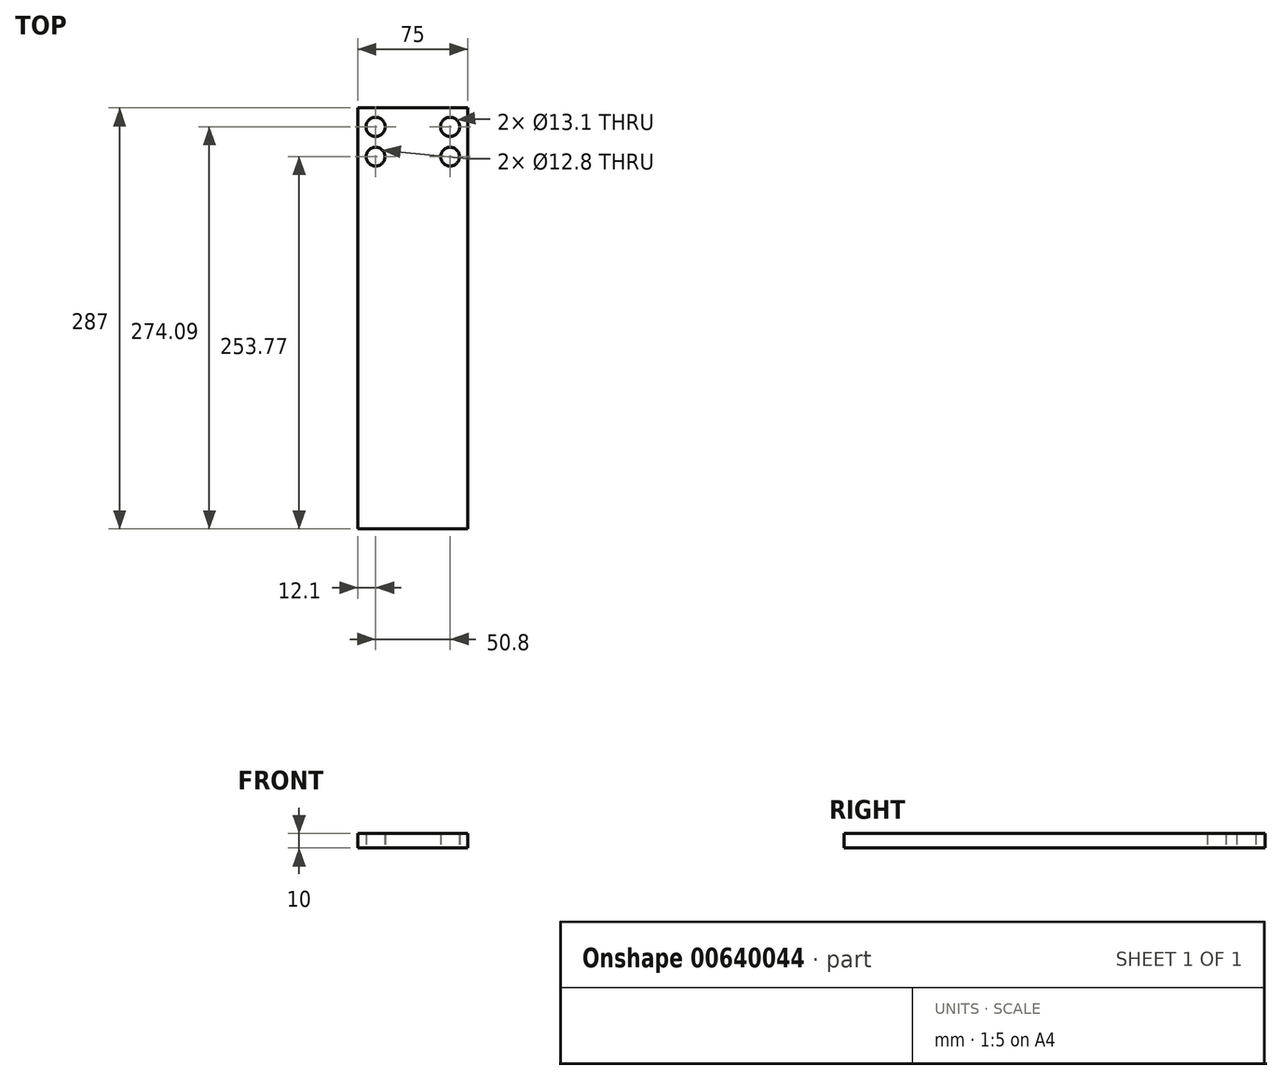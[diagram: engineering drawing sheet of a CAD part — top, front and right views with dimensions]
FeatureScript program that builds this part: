
annotation { "Feature Type Name" : "Feature", "Feature Type Description" : "" }
export const myFeature = defineFeature(function(context is Context, id is Id, definition is map)
    precondition{}
    {
        {
            var Q0;
            Q0=qCreatedBy(makeId("Top.planeOp"),FACE);
            var sketch = newSketch(context, id + "F0", { "sketchPlane" : qUnion([Q0])});
            skLineSegment(sketch, "E0.bottom", {"start": v(-37.5, 143.5) * mm, "end": v(37.5, 143.5) * mm});
            skLineSegment(sketch, "E0.top", {"start": v(-37.5, -143.5) * mm, "end": v(37.5, -143.5) * mm});
            skLineSegment(sketch, "E0.left", {"start": v(-37.5, 143.5) * mm, "end": v(-37.5, -143.5) * mm});
            skLineSegment(sketch, "E0.right", {"start": v(37.5, 143.5) * mm, "end": v(37.5, -143.5) * mm});
            skPoint(sketch, "E0.middle", {"position": v(0, 0) * mm});
            skCircle(sketch, "E1", {"center": v(25.4, 130.6) * mm, "radius": 6.55 * mm});
            skCircle(sketch, "E2", {"center": v(25.4, 110.27) * mm, "radius": 6.4 * mm});
            skCircle(sketch, "E3.MirrorC", {"center": v(-25.4, 130.6) * mm, "radius": 6.55 * mm});
            skCircle(sketch, "E4.MirrorC", {"center": v(-25.4, 110.27) * mm, "radius": 6.4 * mm});
            skSolve(sketch);
        }
        {
            var Q0;
            Q0=makeQuery(id+"F0.imprint","IMPRINT",FACE,{"disambiguationData":[TD([[makeQuery(id+"F0.imprint","IMPRINT",EDGE,{"derivedFrom":sQuery(id+"F0.wireOp",EDGE,"E0.bottom")}),-1.0]])]});
            extrude(context, id + "F1", {"entities" : qUnion([Q0]), "depth" : 10 * mm, "offsetDistance" : 25 * mm});
        }
    });
